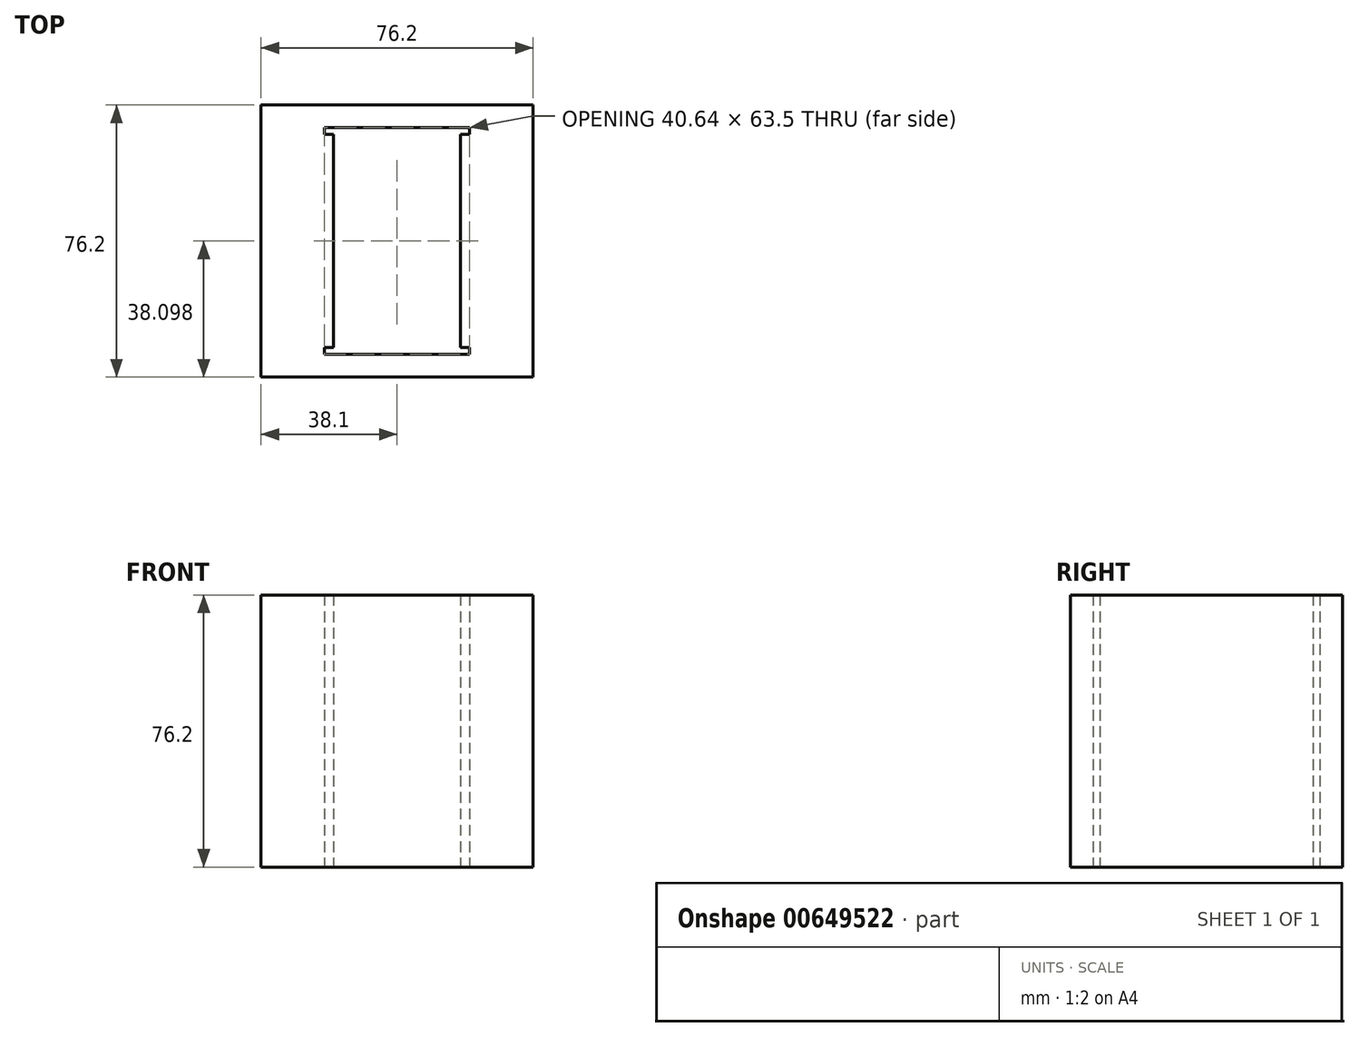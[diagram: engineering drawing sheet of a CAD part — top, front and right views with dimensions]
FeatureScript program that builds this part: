
annotation { "Feature Type Name" : "Feature", "Feature Type Description" : "" }
export const myFeature = defineFeature(function(context is Context, id is Id, definition is map)
    precondition{}
    {
        {
            var Q0;
            Q0=qCreatedBy(makeId("Top.planeOp"),FACE);
            var sketch = newSketch(context, id + "F0", { "sketchPlane" : qUnion([Q0])});
            skLineSegment(sketch, "E0.bottom", {"start": v(0, 0) * mm, "end": v(-76.2, 0) * mm});
            skLineSegment(sketch, "E0.top", {"start": v(0, 76.2) * mm, "end": v(-76.2, 76.2) * mm});
            skLineSegment(sketch, "E0.left", {"start": v(0, 0) * mm, "end": v(0, 76.2) * mm});
            skLineSegment(sketch, "E0.right", {"start": v(-76.2, 0) * mm, "end": v(-76.2, 76.2) * mm});
            skLineSegment(sketch, "E1.bottom", {"start": v(-17.78, 69.85) * mm, "end": v(-58.42, 69.85) * mm});
            skLineSegment(sketch, "E1.top", {"start": v(-17.78, 6.35) * mm, "end": v(-58.42, 6.35) * mm});
            skLineSegment(sketch, "E1.left", {"start": v(-17.78, 69.85) * mm, "end": v(-17.78, 6.35) * mm});
            skLineSegment(sketch, "E1.right", {"start": v(-58.42, 69.85) * mm, "end": v(-58.42, 6.35) * mm});
            skPoint(sketch, "E1.middle", {"position": v(-38.1, 38.1) * mm});
            skPoint(sketch, "E1.middle.positionSnap0", {"position": v(-38.1, 76.2) * mm});
            skPoint(sketch, "E1.middle.positionSnap1", {"position": v(0, 38.1) * mm});
            skPoint(sketch, "E1.centerSnap0", {"position": v(-38.1, 76.2) * mm});
            skPoint(sketch, "E1.centerSnap1", {"position": v(0, 38.1) * mm});
            skLineSegment(sketch, "E2.left", {"start": v(-20.32, 67.95) * mm, "end": v(-20.32, 8.25) * mm});
            skLineSegment(sketch, "E2.right", {"start": v(-55.88, 67.95) * mm, "end": v(-55.88, 8.25) * mm});
            skLineSegment(sketch, "E3.bottom", {"start": v(-20.32, 67.95) * mm, "end": v(-17.78, 67.95) * mm});
            skLineSegment(sketch, "E3.top", {"start": v(-20.32, 8.25) * mm, "end": v(-17.78, 8.25) * mm});
            skLineSegment(sketch, "E4.bottom", {"start": v(-55.88, 67.95) * mm, "end": v(-58.42, 67.95) * mm});
            skLineSegment(sketch, "E4.top", {"start": v(-55.88, 8.25) * mm, "end": v(-58.42, 8.25) * mm});
            skSolve(sketch);
        }
        {
            var Q0;
            Q0=makeQuery(id+"F0.imprint","IMPRINT",FACE,{"disambiguationData":[TD([[makeQuery(id+"F0.imprint","IMPRINT",EDGE,{"derivedFrom":sQuery(id+"F0.wireOp",EDGE,"E0.bottom")}),-1.0]])]});
            var Q1;
            Q1=makeQuery(id+"F0.imprint","IMPRINT",FACE,{"disambiguationData":[TD([[makeQuery(id+"F0.imprint","IMPRINT",EDGE,{"derivedFrom":sQuery(id+"F0.wireOp",EDGE,"E2.right")}),-1.0]])]});
            var Q2;
            Q2=makeQuery(id+"F0.imprint","IMPRINT",FACE,{"disambiguationData":[TD([[makeQuery(id+"F0.imprint","IMPRINT",EDGE,{"derivedFrom":sQuery(id+"F0.wireOp",EDGE,"E2.left")}),1.0]])]});
            extrude(context, id + "F1", {"entities" : qUnion([Q0, Q1, Q2]), "depth" : 76.2 * mm, "offsetDistance" : 25.4 * mm});
        }
        {
            var Q0;
            Q0=qCreatedBy(makeId("Front.planeOp"),FACE);
            var sketch = newSketch(context, id + "F2", { "sketchPlane" : qUnion([Q0])});
            skLineSegment(sketch, "E5", {"start": v(0, 0) * mm, "end": v(0, -50.8) * mm});
            skLineSegment(sketch, "E6", {"start": v(0, 0) * mm, "end": v(0, 76.2) * mm});
            skLineSegment(sketch, "E7", {"start": v(0, 76.2) * mm, "end": v(63.5, 76.2) * mm});
            skLineSegment(sketch, "E8", {"start": v(0, 76.2) * mm, "end": v(-63.5, 76.2) * mm});
            skFitSpline(sketch, "E9", {"points": [v(0, -50.8) * mm, v(63.5, 76.2) * mm], "startDerivative": vector(94.03, 0.81) * mm, "endDerivative": vector(4.04, 146.87) * mm});
            skFitSpline(sketch, "E10", {"points": [v(0, -50.8) * mm, v(-63.5, 76.2) * mm], "startDerivative": vector(-100.7, 2.6) * mm, "endDerivative": vector(0.84, 145.97) * mm});
            skFitSpline(sketch, "E11", {"points": [v(0, -44.45) * mm, v(57.15, 76.2) * mm], "startDerivative": vector(76.81, 2.18) * mm, "endDerivative": vector(4.04, 146.87) * mm});
            skFitSpline(sketch, "E12", {"points": [v(0, -44.45) * mm, v(-57.15, 76.2) * mm], "startDerivative": vector(-79.82, 5.62) * mm, "endDerivative": vector(0.84, 145.97) * mm});
            skSolve(sketch);
        }
        {
            var Q0;
            Q0=makeQuery(id+"F1.opExtrude","SWEPT_BODY",BODY,{"disambiguationData":[OSD([sQuery(id+"F0.wireOp",EDGE,"E0.bottom"),sQuery(id+"F0.wireOp",EDGE,"E0.top"),sQuery(id+"F0.wireOp",EDGE,"E0.left"),sQuery(id+"F0.wireOp",EDGE,"E0.right"),sQuery(id+"F0.wireOp",EDGE,"E1.bottom"),sQuery(id+"F0.wireOp",EDGE,"E1.top"),sQuery(id+"F0.wireOp",EDGE,"E1.left"),sQuery(id+"F0.wireOp",EDGE,"E1.right"),sQuery(id+"F0.wireOp",EDGE,"E2.left"),sQuery(id+"F0.wireOp",EDGE,"E2.right"),sQuery(id+"F0.wireOp",EDGE,"E3.bottom"),sQuery(id+"F0.wireOp",EDGE,"E3.top"),sQuery(id+"F0.wireOp",EDGE,"E4.bottom"),sQuery(id+"F0.wireOp",EDGE,"E4.top")])]});
            transform(context, id + "F3", {"entities" : qUnion([Q0]), "transformType" : TransformType.TRANSLATION_3D, "dx" : 0 * mm, "dy" : 106.93 * mm, "dz" : 0 * mm, "makeCopy" : false});
        }
        {
            var Q0;
            {var subQ0=sQuery(id+"F2.wireOp",EDGE,"E6");Q0=makeQuery(id+"F2.imprint","IMPRINT",FACE,{"disambiguationData":[TD([[makeQuery(id+"F2.imprint","IMPRINT",EDGE,{"derivedFrom":subQ0}),1.0]])]});}
            var Q1;
            {var subQ0=sQuery(id+"F2.wireOp",EDGE,"E6");Q1=makeQuery(id+"F2.imprint","IMPRINT",FACE,{"disambiguationData":[TD([[makeQuery(id+"F2.imprint","IMPRINT",EDGE,{"derivedFrom":subQ0}),-1.0]])]});}
            var Q2;
            Q2=sQuery(id+"F2.wireOp",EDGE,"E9");
            var Q3;
            Q3=sQuery(id+"F2.wireOp",EDGE,"E11");
            var Q4;
            Q4=sQuery(id+"F2.wireOp",EDGE,"E5");
            revolve(context, id + "F4", {"bodyType" : ToolBodyType.SURFACE, "operationType" : NewBodyOperationType.ADD, "entities" : qUnion([Q0, Q1]), "surfaceEntities" : qUnion([Q2, Q3]), "axis" : qUnion([Q4]), "revolveType" : RevolveType.FULL, "oppositeDirection" : true});
        }
        {
            var Q0;
            Q0=makeQuery(id+"F4.opRevolve","SWEPT_BODY",BODY,{"disambiguationData":[OSD([sQuery(id+"F2.wireOp",EDGE,"E9")])]});
            var Q1;
            Q1=makeQuery(id+"F4.opRevolve","SWEPT_BODY",BODY,{"disambiguationData":[OSD([sQuery(id+"F2.wireOp",EDGE,"E11")])]});
            var Q2;
            Q2=qCreatedBy(makeId("Origin.pointOp"),VERTEX);
            transform(context, id + "F5", {"entities" : qUnion([Q0, Q1]), "transformType" : TransformType.SCALE_UNIFORMLY, "scale" : 1.15, "scalePoint" : qUnion([Q2]), "makeCopy" : false});
        }
        {
            var Q0;
            Q0=makeQuery(id+"F1.opExtrude","SWEPT_BODY",BODY,{"disambiguationData":[OSD([sQuery(id+"F0.wireOp",EDGE,"E0.bottom"),sQuery(id+"F0.wireOp",EDGE,"E0.top"),sQuery(id+"F0.wireOp",EDGE,"E0.left"),sQuery(id+"F0.wireOp",EDGE,"E0.right"),sQuery(id+"F0.wireOp",EDGE,"E1.bottom"),sQuery(id+"F0.wireOp",EDGE,"E1.top"),sQuery(id+"F0.wireOp",EDGE,"E1.left"),sQuery(id+"F0.wireOp",EDGE,"E1.right"),sQuery(id+"F0.wireOp",EDGE,"E2.left"),sQuery(id+"F0.wireOp",EDGE,"E2.right"),sQuery(id+"F0.wireOp",EDGE,"E3.bottom"),sQuery(id+"F0.wireOp",EDGE,"E3.top"),sQuery(id+"F0.wireOp",EDGE,"E4.bottom"),sQuery(id+"F0.wireOp",EDGE,"E4.top")])]});
            transform(context, id + "F6", {"entities" : qUnion([Q0]), "transformType" : TransformType.TRANSLATION_3D, "dx" : 38.1 * mm, "dy" : -144.53 * mm, "dz" : 11.94 * mm, "makeCopy" : false});
        }
    });
